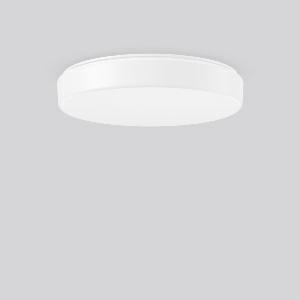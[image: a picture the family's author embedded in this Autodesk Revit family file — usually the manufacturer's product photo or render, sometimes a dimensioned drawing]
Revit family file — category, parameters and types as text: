
# Revit family: flat_polymero_kreis_672392_002_1_89_2179
name_source: partatom
category: Lighting Fixtures
units: mm (PartAtom-declared; Revit-internal decimal feet)

## family parameters
Cut with Voids When Loaded = No
Host = Face
Light Source = No
Part Type = Normal
Room Calculation Point = No
Round Connector Dimension = Use Diameter
Shared = No

## types (1)
- FLAT POLYMERO KREIS (1 x LED Modul 840, 2600 lm, 4000)
    Apparent Load = 24 VA
    CIE Flux Codes = 42 72 91 84 100
    Color Rendering = 80
    Color Temperature = 4000
    Default Elevation = 1800 mm
    Description = Series: FLAT POLYMERO KREIS
Decorative round surface-mounted luminaire. For escape route illumination. Base: metal, powder-coated. Diffuser made of non-yellowing plastic (PMMA), opal. Diffuser fastening: patented push system. Suitable for Ceiling mounting, Wall (surface). Driver integrated. Suitable for connection to central battery systems. With AC Control monitoring module for LUXIFAIR central battery units. 
Colour: white
Diameter: 515 mm
Height: 98 mm
Weight: 2.86 kg
Operating mode: Non-maintained power mode and maintained power mode
Lamp: LED
Socket: without socket
Colour temperature: 4000K
Colour rendering index (CRI): 80
System power: 24 W
Rated luminous flux: 2600 lm
Luminous flux, emergency: 550 lm
System power, emergency: 6.9 W
Control gear: Regulated power supply
Protection class: I
Type of protection: IP 40
    Height = 98 mm
    Lamp = 1 x LED Modul 840
    Lamp Light Flux = 2600 lm
    Lamp count = 1
    Length = 515 mm
    Lifetime = 50000 h
    Luminous efficacy = 108 lm/W
    Manufacturer = RZB
    ModVariant = No
    Model = 672392.002.1.89
    Mounting Place = Ceiling, Wall
    Mounting Type = Surface mounted
    Number of Poles = 1
    OnlyDefault = Yes
    Power Factor = 1
    Product Name = FLAT POLYMERO KREIS
    Product group = Surface mounted ceiling and wall luminaires
    ProductGroupID = 305
    Protection Class = Protection class I
    Protection Degree = IP 40
    RLX_Detail_Level = 1
    RLX_Emergency_Light_Flux = 550 lm
    RLX_Emergency_Type = 3
    RLX_Emergency_Type_DB = Yes
    RlxData = <blob elided: 57069 chars, md5=352808c6>
    Socket = socket
    Standby Power = 0 W
    System Light Flux = 2600 lm
    System Power = 24 W
    Type Comments = Product without accessories
    Type Image = 311604.862.79.jpg
    URL = http://relux.com
    VarID = ---
    Voltage = 230 V
    Voltage Range = 220-240 V
    Weight = 0.00 kg
    Width = 0 mm  [stored 0 ft]

note: [stored X ft] marks values corroborated as IEEE doubles in the binary element streams (Revit-internal decimal feet)

## geometry (parser evidence)
native form markers: Blend x4, Sweep x14
no freeform markers — native parametric forms only
